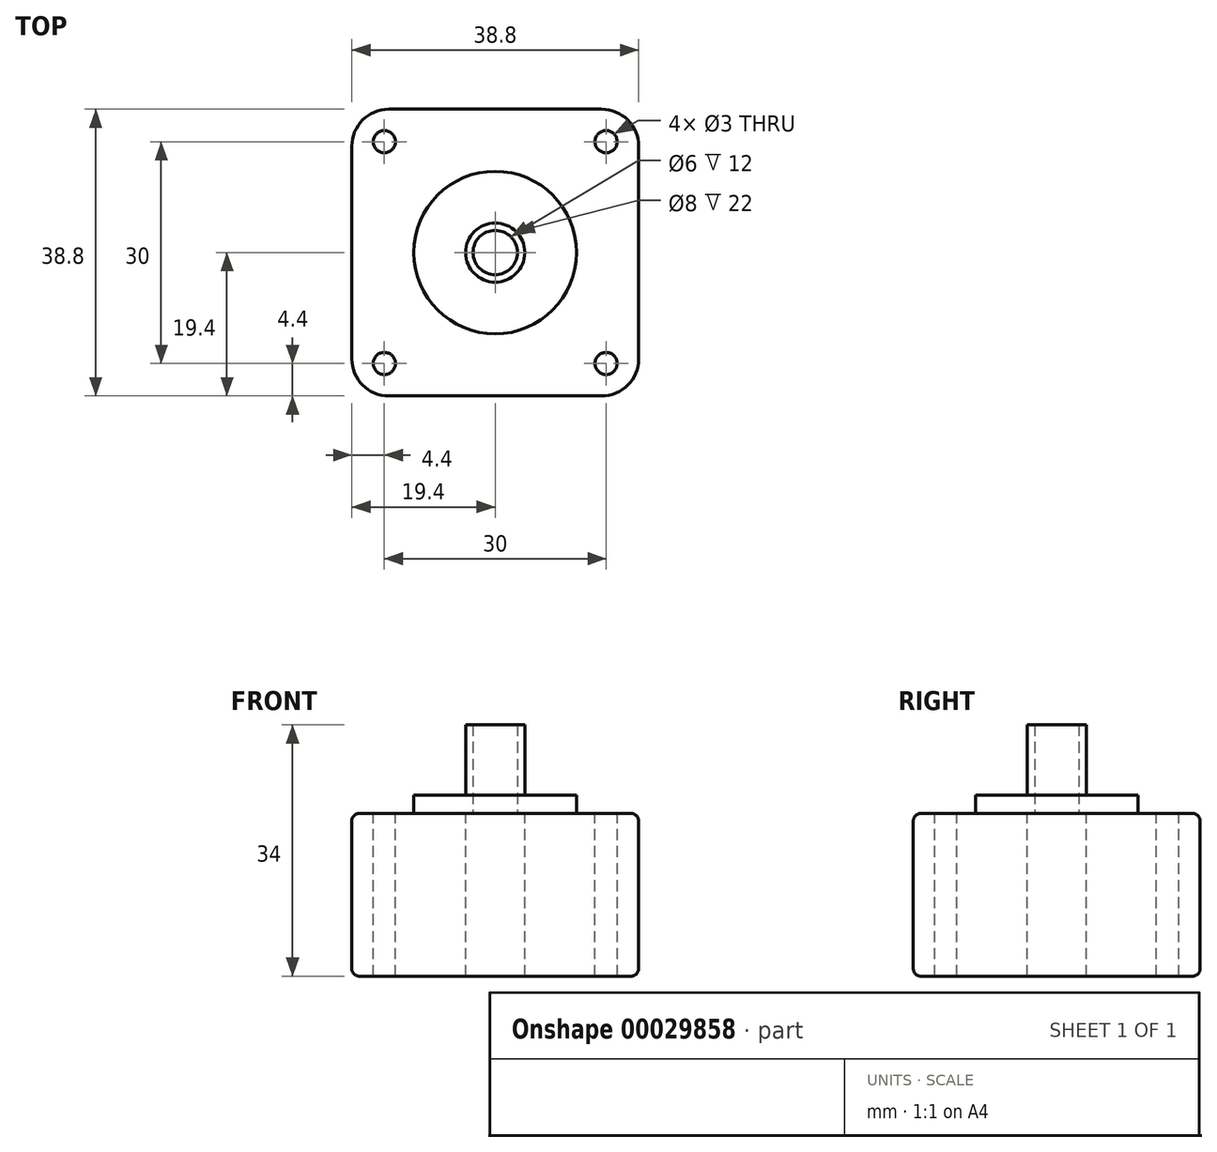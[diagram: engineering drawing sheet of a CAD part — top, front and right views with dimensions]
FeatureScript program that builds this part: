
annotation { "Feature Type Name" : "Feature", "Feature Type Description" : "" }
export const myFeature = defineFeature(function(context is Context, id is Id, definition is map)
    precondition{}
    {
        {
            var Q0;
            Q0=qCreatedBy(makeId("Top.planeOp"),FACE);
            var sketch = newSketch(context, id + "F0", { "sketchPlane" : qUnion([Q0])});
            skCircle(sketch, "E0", {"center": v(0, 0) * mm, "radius": 4 * mm});
            skCircle(sketch, "E1", {"center": v(0, 0) * mm, "radius": 11 * mm});
            skCircle(sketch, "E2", {"center": v(0, 0) * mm, "radius": 3 * mm});
            skCircle(sketch, "E3", {"center": v(-15, 15) * mm, "radius": 1.5 * mm});
            skLineSegment(sketch, "E4", {"start": v(0, 0) * mm, "end": v(0, 27.49) * mm, "construction": true});
            skLineSegment(sketch, "E5", {"start": v(0, 0) * mm, "end": v(27.8, 0) * mm, "construction": true});
            skCircle(sketch, "E6.MirrorC", {"center": v(-15, -15) * mm, "radius": 1.5 * mm});
            skCircle(sketch, "E7.MirrorC", {"center": v(15, 15) * mm, "radius": 1.5 * mm});
            skCircle(sketch, "E8.MirrorC", {"center": v(15, -15) * mm, "radius": 1.5 * mm});
            skLineSegment(sketch, "E9.bottom", {"start": v(-19.4, 19.4) * mm, "end": v(19.4, 19.4) * mm});
            skLineSegment(sketch, "E9.top", {"start": v(-19.4, -19.4) * mm, "end": v(19.4, -19.4) * mm});
            skLineSegment(sketch, "E9.left", {"start": v(-19.4, 19.4) * mm, "end": v(-19.4, -19.4) * mm});
            skLineSegment(sketch, "E9.right", {"start": v(19.4, 19.4) * mm, "end": v(19.4, -19.4) * mm});
            skSolve(sketch);
        }
        {
            var Q0;
            Q0=makeQuery(id+"F0.imprint","IMPRINT",FACE,{"disambiguationData":[TD([[makeQuery(id+"F0.imprint","IMPRINT",EDGE,{"derivedFrom":sQuery(id+"F0.wireOp",EDGE,"E0")}),1.0]])]});
            extrude(context, id + "F1", {"entities" : qUnion([Q0]), "depth" : 12 * mm});
        }
        {
            var Q0;
            Q0=makeQuery(id+"F0.imprint","IMPRINT",FACE,{"disambiguationData":[TD([[makeQuery(id+"F0.imprint","IMPRINT",EDGE,{"derivedFrom":sQuery(id+"F0.wireOp",EDGE,"E1")}),-1.0]])]});
            var Q1;
            Q1=makeQuery(id+"F0.imprint","IMPRINT",FACE,{"disambiguationData":[TD([[makeQuery(id+"F0.imprint","IMPRINT",EDGE,{"derivedFrom":sQuery(id+"F0.wireOp",EDGE,"E0")}),-1.0]])]});
            extrude(context, id + "F2", {"entities" : qUnion([Q0, Q1]), "oppositeDirection" : true, "depth" : 22 * mm});
        }
        {
            var Q0;
            Q0=makeQuery(id+"F0.imprint","IMPRINT",FACE,{"disambiguationData":[TD([[makeQuery(id+"F0.imprint","IMPRINT",EDGE,{"derivedFrom":sQuery(id+"F0.wireOp",EDGE,"E0")}),-1.0]])]});
            extrude(context, id + "F3", {"entities" : qUnion([Q0]), "operationType" : NewBodyOperationType.ADD, "depth" : 2.5 * mm});
        }
        {
            var Q0;
            Q0=makeQuery(id+"F2.opExtrude","SWEPT_EDGE",EDGE,{"disambiguationData":[OSD([sQuery(id+"F0.wireOp",EDGE,"E9.top"),sQuery(id+"F0.wireOp",EDGE,"E9.right")])]});
            var Q1;
            Q1=makeQuery(id+"F2.opExtrude","SWEPT_EDGE",EDGE,{"disambiguationData":[OSD([sQuery(id+"F0.wireOp",EDGE,"E9.top"),sQuery(id+"F0.wireOp",EDGE,"E9.left")])]});
            var Q2;
            Q2=makeQuery(id+"F2.opExtrude","SWEPT_EDGE",EDGE,{"disambiguationData":[OSD([sQuery(id+"F0.wireOp",EDGE,"E9.bottom"),sQuery(id+"F0.wireOp",EDGE,"E9.left")])]});
            var Q3;
            Q3=makeQuery(id+"F2.opExtrude","SWEPT_EDGE",EDGE,{"disambiguationData":[OSD([sQuery(id+"F0.wireOp",EDGE,"E9.bottom"),sQuery(id+"F0.wireOp",EDGE,"E9.right")])]});
            fillet(context, id + "F4", {"entities" : qUnion([Q0, Q1, Q2, Q3]), "radius" : 5 * mm, "tangentPropagation" : true, "allowEdgeOverflow" : false});
        }
        {
            var Q0;
            Q0=makeQuery(id+"F2.opExtrude","CAP_EDGE",EDGE,{"disambiguationData":[OSD([sQuery(id+"F0.wireOp",EDGE,"E9.top")])],"isStart":true});
            var Q1;
            Q1=makeQuery(id+"F2.opExtrude","CAP_EDGE",EDGE,{"disambiguationData":[OSD([sQuery(id+"F0.wireOp",EDGE,"E9.top")])],"isStart":false});
            fillet(context, id + "F5", {"entities" : qUnion([Q0, Q1]), "radius" : 1 * mm, "tangentPropagation" : true, "allowEdgeOverflow" : false});
        }
    });
